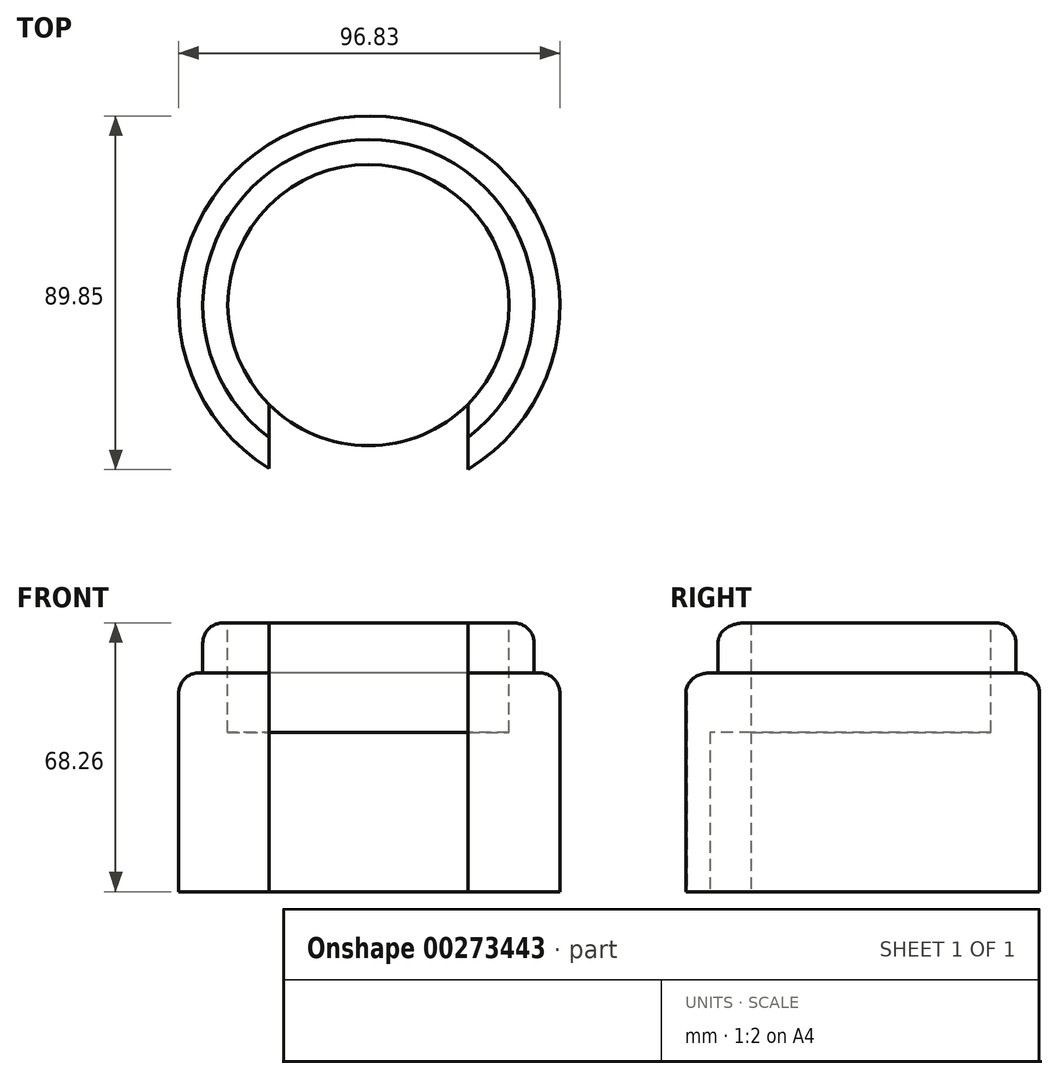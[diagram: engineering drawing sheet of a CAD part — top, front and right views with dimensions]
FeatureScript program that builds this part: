
annotation { "Feature Type Name" : "Feature", "Feature Type Description" : "" }
export const myFeature = defineFeature(function(context is Context, id is Id, definition is map)
    precondition{}
    {
        {
            var Q0;
            Q0=qCreatedBy(makeId("Top.planeOp"),FACE);
            var sketch = newSketch(context, id + "F0", { "sketchPlane" : qUnion([Q0])});
            skCircle(sketch, "E0", {"center": v(0.23, -0.36) * mm, "radius": 48.42 * mm});
            skSolve(sketch);
        }
        {
            var Q0;
            Q0=makeQuery(id+"F0.imprint","IMPRINT",FACE,{"disambiguationData":[TD([[makeQuery(id+"F0.imprint","IMPRINT",EDGE,{"derivedFrom":sQuery(id+"F0.wireOp",EDGE,"E0")}),1.0]])]});
            extrude(context, id + "F1", {"entities" : qUnion([Q0]), "depth" : 55.56 * mm});
        }
        {
            var Q0;
            Q0=makeQuery(id+"F1.opExtrude","CAP_FACE",FACE,{"disambiguationData":[OSD([sQuery(id+"F0.wireOp",EDGE,"E0")])],"isStart":false});
            var sketch = newSketch(context, id + "F2", { "sketchPlane" : qUnion([Q0])});
            skCircle(sketch, "E1", {"center": v(0, 0) * mm, "radius": 42.07 * mm});
            skSolve(sketch);
        }
        {
            var Q0;
            Q0=makeQuery(id+"F2.imprint","IMPRINT",FACE,{"disambiguationData":[TD([[makeQuery(id+"F2.imprint","IMPRINT",EDGE,{"derivedFrom":sQuery(id+"F2.wireOp",EDGE,"E1")}),1.0]])]});
            var Q1;
            Q1=sQuery(id+"F2.wireOp",EDGE,"E1");
            extrude(context, id + "F3", {"entities" : qUnion([Q0]), "operationType" : NewBodyOperationType.ADD, "surfaceEntities" : qUnion([Q1]), "depth" : 12.7 * mm});
        }
        {
            var Q0;
            Q0=makeQuery(id+"F3.opExtrude","CAP_FACE",FACE,{"disambiguationData":[OSD([sQuery(id+"F2.wireOp",EDGE,"E1")])],"isStart":false});
            var sketch = newSketch(context, id + "F4", { "sketchPlane" : qUnion([Q0])});
            skCircle(sketch, "E2", {"center": v(0, 0) * mm, "radius": 35.72 * mm});
            skSolve(sketch);
        }
        {
            var Q0;
            Q0=makeQuery(id+"F4.imprint","IMPRINT",FACE,{"disambiguationData":[TD([[makeQuery(id+"F4.imprint","IMPRINT",EDGE,{"derivedFrom":sQuery(id+"F4.wireOp",EDGE,"E2")}),1.0]])]});
            var Q1;
            Q1=sQuery(id+"F4.wireOp",EDGE,"E2");
            extrude(context, id + "F5", {"entities" : qUnion([Q0]), "operationType" : NewBodyOperationType.REMOVE, "surfaceEntities" : qUnion([Q1]), "oppositeDirection" : true, "depth" : 27.78 * mm});
        }
        {
            var Q0;
            Q0=makeQuery(id+"F1.opExtrude","CAP_EDGE",EDGE,{"disambiguationData":[OSD([sQuery(id+"F0.wireOp",EDGE,"E0")])],"isStart":false});
            var Q1;
            Q1=makeQuery(id+"F3.opExtrude","CAP_EDGE",EDGE,{"disambiguationData":[OSD([sQuery(id+"F2.wireOp",EDGE,"E1")])],"isStart":false});
            fillet(context, id + "F6", {"entities" : qUnion([Q0, Q1]), "radius" : 5.08 * mm, "tangentPropagation" : true, "allowEdgeOverflow" : false});
        }
        {
            var Q0;
            Q0=qCreatedBy(makeId("Top.planeOp"),FACE);
            var sketch = newSketch(context, id + "F7", { "sketchPlane" : qUnion([Q0])});
            skCircle(sketch, "E3", {"center": v(0, 0) * mm, "radius": 35.72 * mm});
            skLineSegment(sketch, "E4.bottom", {"start": v(0, -55.84) * mm, "end": v(-25.28, -55.84) * mm});
            skLineSegment(sketch, "E4.top", {"start": v(0, -25.23) * mm, "end": v(-25.28, -25.23) * mm});
            skLineSegment(sketch, "E4.left", {"start": v(0, -55.84) * mm, "end": v(0, -25.23) * mm});
            skLineSegment(sketch, "E4.right", {"start": v(-25.28, -55.84) * mm, "end": v(-25.28, -25.23) * mm});
            skLineSegment(sketch, "E5.MirrorCS", {"start": v(0, -25.23) * mm, "end": v(25.28, -25.23) * mm});
            skLineSegment(sketch, "E6.MirrorCS", {"start": v(25.28, -55.84) * mm, "end": v(25.28, -25.23) * mm});
            skLineSegment(sketch, "E7.MirrorCS", {"start": v(0, -55.84) * mm, "end": v(25.28, -55.84) * mm});
            skSolve(sketch);
        }
        {
            var Q0;
            {var subQ0=sQuery(id+"F7.wireOp",EDGE,"E6.MirrorCS");Q0=makeQuery(id+"F7.imprint","IMPRINT",FACE,{"disambiguationData":[TD([[makeQuery(id+"F7.imprint","IMPRINT",EDGE,{"derivedFrom":subQ0}),1.0]])]});}
            var Q1;
            {var subQ4=sQuery(id+"F7.wireOp",EDGE,"E4.bottom");Q1=makeQuery(id+"F7.imprint","IMPRINT",FACE,{"disambiguationData":[TD([[makeQuery(id+"F7.imprint","IMPRINT",EDGE,{"derivedFrom":subQ4}),-1.0]])]});}
            extrude(context, id + "F8", {"entities" : qUnion([Q0, Q1]), "operationType" : NewBodyOperationType.REMOVE, "depth" : 100.08 * mm});
        }
    });
